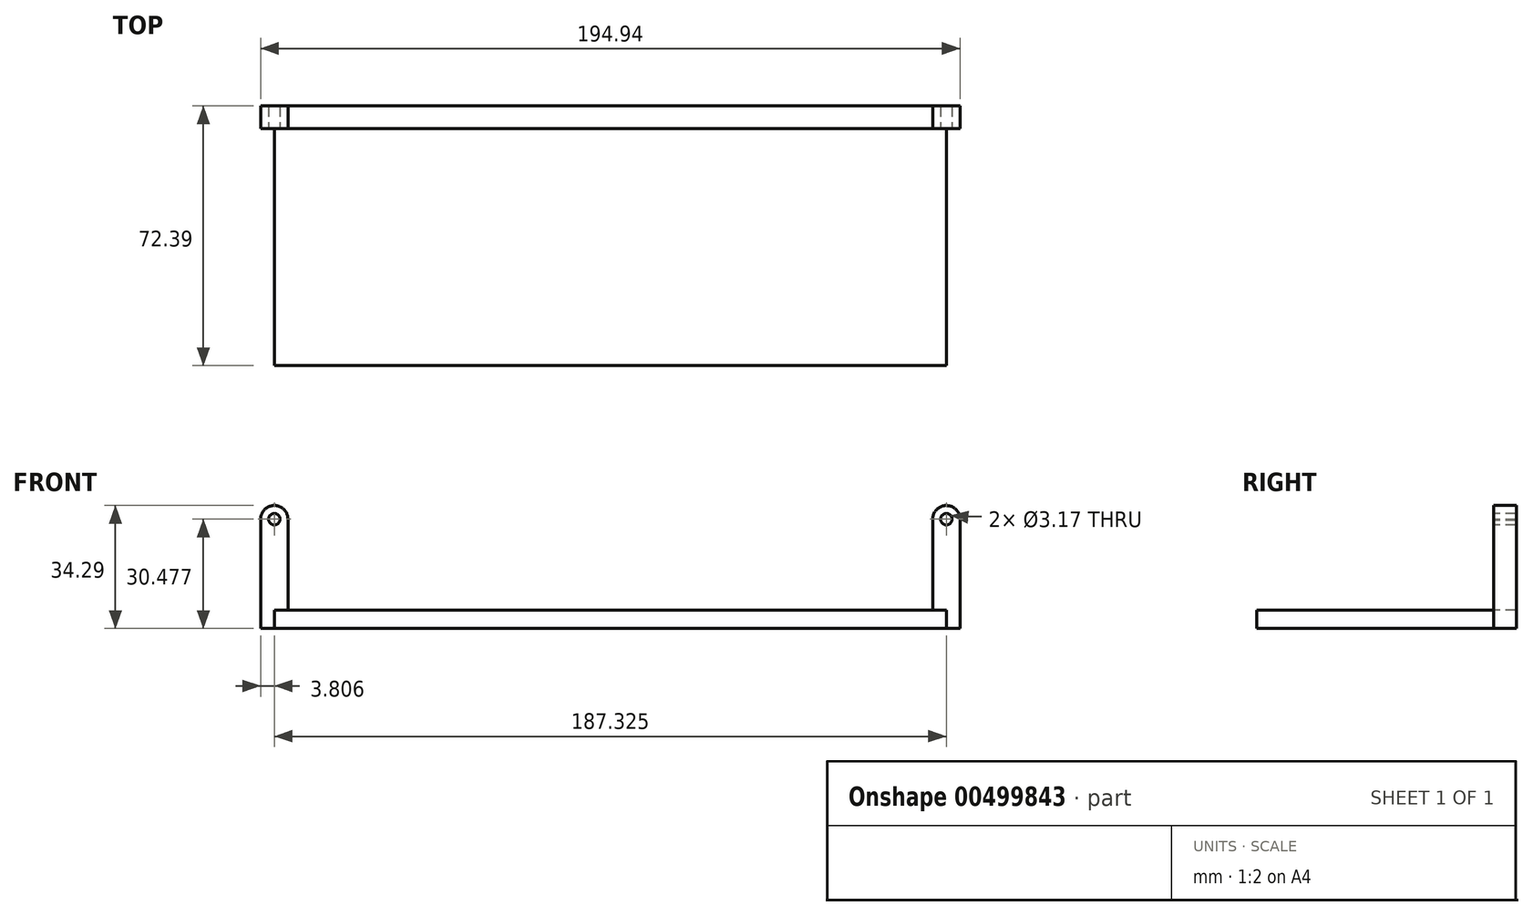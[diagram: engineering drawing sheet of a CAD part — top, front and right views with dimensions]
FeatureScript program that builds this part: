
annotation { "Feature Type Name" : "Feature", "Feature Type Description" : "" }
export const myFeature = defineFeature(function(context is Context, id is Id, definition is map)
    precondition{}
    {
        {
            var Q0;
            Q0=qCreatedBy(makeId("Front.planeOp"),FACE);
            var sketch = newSketch(context, id + "F0", { "sketchPlane" : qUnion([Q0])});
            skLineSegment(sketch, "E0.bottom", {"start": v(-88.22, 1.32) * mm, "end": v(99.1, 1.32) * mm});
            skLineSegment(sketch, "E0.top", {"start": v(-88.22, -3.76) * mm, "end": v(99.1, -3.76) * mm});
            skLineSegment(sketch, "E0.left", {"start": v(-88.22, 1.32) * mm, "end": v(-88.22, -3.76) * mm});
            skLineSegment(sketch, "E0.right", {"start": v(99.1, 1.32) * mm, "end": v(99.1, -3.76) * mm});
            skCircle(sketch, "E1", {"center": v(-88.22, 26.72) * mm, "radius": 1.59 * mm});
            skCircle(sketch, "E2", {"center": v(99.1, 26.72) * mm, "radius": 1.59 * mm});
            skLineSegment(sketch, "E3", {"start": v(102.91, 26.72) * mm, "end": v(102.91, -3.76) * mm});
            skLineSegment(sketch, "E4", {"start": v(-92.03, 26.72) * mm, "end": v(-92.03, -3.76) * mm});
            skCircle(sketch, "E5", {"center": v(-88.22, 26.72) * mm, "radius": 3.8 * mm});
            skCircle(sketch, "E6", {"center": v(99.1, 26.72) * mm, "radius": 3.8 * mm});
            skLineSegment(sketch, "E7", {"start": v(-88.22, -3.76) * mm, "end": v(-92.03, -3.76) * mm});
            skLineSegment(sketch, "E8", {"start": v(99.1, -3.76) * mm, "end": v(102.91, -3.76) * mm});
            skLineSegment(sketch, "E9", {"start": v(-84.43, 26.42) * mm, "end": v(-84.43, -3.76) * mm});
            skLineSegment(sketch, "E10", {"start": v(95.3, 26.63) * mm, "end": v(95.3, -3.76) * mm});
            skSolve(sketch);
        }
        {
            var Q0;
            {var subQ0=sQuery(id+"F0.wireOp",EDGE,"E9");var subQ1=sQuery(id+"F0.wireOp",EDGE,"E0.bottom");var subQ2=makeQuery(id+"F0.imprint","INTERSECT",VERTEX,{"derivedFrom":[subQ1,subQ0]});Q0=makeQuery(id+"F0.imprint","IMPRINT",FACE,{"disambiguationData":[TD([[makeQuery(id+"F0.imprint","IMPRINT",EDGE,{"disambiguationData":[TD([[subQ2,-1.0]])],"derivedFrom":subQ1}),-1.0]])]});}
            var Q1;
            {var subQ0=sQuery(id+"F0.wireOp",EDGE,"E0.left");Q1=makeQuery(id+"F0.imprint","IMPRINT",FACE,{"disambiguationData":[TD([[makeQuery(id+"F0.imprint","IMPRINT",EDGE,{"derivedFrom":subQ0}),1.0]])]});}
            var Q2;
            {var subQ0=sQuery(id+"F0.wireOp",EDGE,"E0.right");Q2=makeQuery(id+"F0.imprint","IMPRINT",FACE,{"disambiguationData":[TD([[makeQuery(id+"F0.imprint","IMPRINT",EDGE,{"derivedFrom":subQ0}),-1.0]])]});}
            extrude(context, id + "F1", {"entities" : qUnion([Q0, Q1, Q2]), "depth" : 66.04 * mm});
        }
        {
            var Q0;
            {var subQ4=sQuery(id+"F0.wireOp",EDGE,"E0.right");Q0=makeQuery(id+"F0.imprint","IMPRINT",FACE,{"disambiguationData":[TD([[makeQuery(id+"F0.imprint","IMPRINT",EDGE,{"derivedFrom":subQ4}),1.0]])]});}
            var Q1;
            Q1=makeQuery(id+"F0.imprint","IMPRINT",FACE,{"disambiguationData":[TD([[makeQuery(id+"F0.imprint","IMPRINT",EDGE,{"derivedFrom":sQuery(id+"F0.wireOp",EDGE,"E2")}),-1.0]])]});
            var Q2;
            Q2=makeQuery(id+"F0.imprint","IMPRINT",FACE,{"disambiguationData":[TD([[makeQuery(id+"F0.imprint","IMPRINT",EDGE,{"derivedFrom":sQuery(id+"F0.wireOp",EDGE,"E1")}),-1.0]])]});
            var Q3;
            {var subQ4=sQuery(id+"F0.wireOp",EDGE,"E0.left");Q3=makeQuery(id+"F0.imprint","IMPRINT",FACE,{"disambiguationData":[TD([[makeQuery(id+"F0.imprint","IMPRINT",EDGE,{"derivedFrom":subQ4}),-1.0]])]});}
            var Q4;
            {var subQ0=sQuery(id+"F0.wireOp",EDGE,"E9");var subQ1=sQuery(id+"F0.wireOp",EDGE,"E0.bottom");var subQ2=makeQuery(id+"F0.imprint","INTERSECT",VERTEX,{"derivedFrom":[subQ1,subQ0]});Q4=makeQuery(id+"F0.imprint","IMPRINT",FACE,{"disambiguationData":[TD([[makeQuery(id+"F0.imprint","IMPRINT",EDGE,{"disambiguationData":[TD([[subQ2,-1.0]])],"derivedFrom":subQ1}),-1.0]])]});}
            var Q5;
            {var subQ0=sQuery(id+"F0.wireOp",EDGE,"E0.left");Q5=makeQuery(id+"F0.imprint","IMPRINT",FACE,{"disambiguationData":[TD([[makeQuery(id+"F0.imprint","IMPRINT",EDGE,{"derivedFrom":subQ0}),1.0]])]});}
            var Q6;
            {var subQ0=sQuery(id+"F0.wireOp",EDGE,"E0.right");Q6=makeQuery(id+"F0.imprint","IMPRINT",FACE,{"disambiguationData":[TD([[makeQuery(id+"F0.imprint","IMPRINT",EDGE,{"derivedFrom":subQ0}),-1.0]])]});}
            extrude(context, id + "F2", {"entities" : qUnion([Q0, Q1, Q2, Q3, Q4, Q5, Q6]), "oppositeDirection" : true, "depth" : 6.35 * mm});
        }
    });
